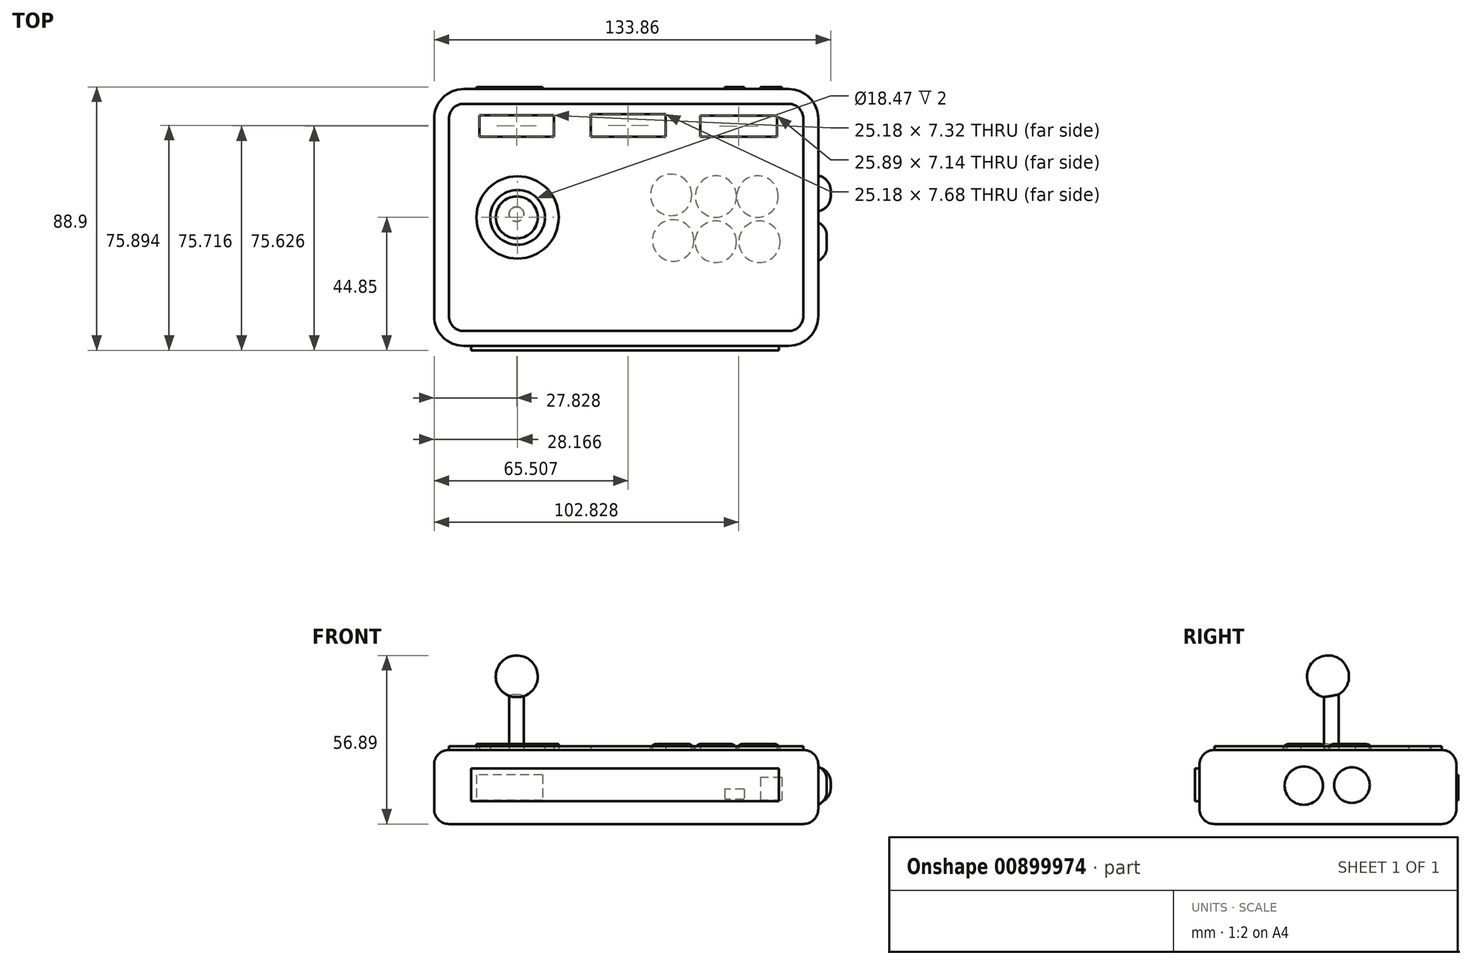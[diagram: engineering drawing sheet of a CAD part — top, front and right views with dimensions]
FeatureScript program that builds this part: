
annotation { "Feature Type Name" : "Feature", "Feature Type Description" : "" }
export const myFeature = defineFeature(function(context is Context, id is Id, definition is map)
    precondition{}
    {
        {
            var Q0;
            Q0=qCreatedBy(makeId("Top.planeOp"),FACE);
            var sketch = newSketch(context, id + "F0", { "sketchPlane" : qUnion([Q0])});
            skLineSegment(sketch, "E0.bottom", {"start": v(64.83, -43.35) * mm, "end": v(-64.83, -43.35) * mm});
            skLineSegment(sketch, "E0.top", {"start": v(64.83, 43.35) * mm, "end": v(-64.83, 43.35) * mm});
            skLineSegment(sketch, "E0.left", {"start": v(64.83, -43.35) * mm, "end": v(64.83, 43.35) * mm});
            skLineSegment(sketch, "E0.right", {"start": v(-64.83, -43.35) * mm, "end": v(-64.83, 43.35) * mm});
            skPoint(sketch, "E0.middle", {"position": v(0, 0) * mm});
            skSolve(sketch);
        }
        {
            var Q0;
            Q0 = qSketchRegion(id + "F0", true);
            extrude(context, id + "F1", {"entities" : qUnion([Q0]), "depth" : 25 * mm, "offsetDistance" : 25 * mm});
        }
        {
            var Q0;
            Q0=makeQuery(id+"F1.opExtrude","SWEPT_EDGE",EDGE,{"disambiguationData":[OSD([sQuery(id+"F0.wireOp",EDGE,"E0.bottom"),sQuery(id+"F0.wireOp",EDGE,"E0.right")])]});
            var Q1;
            Q1=makeQuery(id+"F1.opExtrude","SWEPT_EDGE",EDGE,{"disambiguationData":[OSD([sQuery(id+"F0.wireOp",EDGE,"E0.top"),sQuery(id+"F0.wireOp",EDGE,"E0.right")])]});
            var Q2;
            Q2=makeQuery(id+"F1.opExtrude","SWEPT_EDGE",EDGE,{"disambiguationData":[OSD([sQuery(id+"F0.wireOp",EDGE,"E0.bottom"),sQuery(id+"F0.wireOp",EDGE,"E0.left")])]});
            var Q3;
            Q3=makeQuery(id+"F1.opExtrude","SWEPT_EDGE",EDGE,{"disambiguationData":[OSD([sQuery(id+"F0.wireOp",EDGE,"E0.top"),sQuery(id+"F0.wireOp",EDGE,"E0.left")])]});
            fillet(context, id + "F2", {"entities" : qUnion([Q0, Q1, Q2, Q3]), "radius" : 10 * mm, "tangentPropagation" : true, "allowEdgeOverflow" : false});
        }
        {
            var Q0;
            Q0=makeQuery(id+"F1.opExtrude","CAP_FACE",FACE,{"disambiguationData":[OSD([sQuery(id+"F0.wireOp",EDGE,"E0.bottom"),sQuery(id+"F0.wireOp",EDGE,"E0.top"),sQuery(id+"F0.wireOp",EDGE,"E0.left"),sQuery(id+"F0.wireOp",EDGE,"E0.right")])],"isStart":false});
            var Q1;
            Q1=makeQuery(id+"F1.opExtrude","CAP_FACE",FACE,{"disambiguationData":[OSD([sQuery(id+"F0.wireOp",EDGE,"E0.bottom"),sQuery(id+"F0.wireOp",EDGE,"E0.top"),sQuery(id+"F0.wireOp",EDGE,"E0.left"),sQuery(id+"F0.wireOp",EDGE,"E0.right")])],"isStart":true});
            fillet(context, id + "F3", {"entities" : qUnion([Q0, Q1]), "radius" : 5 * mm, "tangentPropagation" : true, "allowEdgeOverflow" : false});
        }
        {
            var Q0;
            Q0=makeQuery(id+"F1.opExtrude","CAP_FACE",FACE,{"disambiguationData":[OSD([sQuery(id+"F0.wireOp",EDGE,"E0.bottom"),sQuery(id+"F0.wireOp",EDGE,"E0.top"),sQuery(id+"F0.wireOp",EDGE,"E0.left"),sQuery(id+"F0.wireOp",EDGE,"E0.right")])],"isStart":false});
            var sketch = newSketch(context, id + "F4", { "sketchPlane" : qUnion([Q0])});
            skCircle(sketch, "E1", {"center": v(-36.66, 0) * mm, "radius": 9.23 * mm});
            skCircle(sketch, "E2", {"center": v(-36.66, 0) * mm, "radius": 13.9 * mm});
            skCircle(sketch, "E3", {"center": v(15.89, -7.78) * mm, "radius": 7 * mm});
            skCircle(sketch, "E4", {"center": v(30.25, -8.22) * mm, "radius": 7 * mm});
            skCircle(sketch, "E5", {"center": v(45, -8.22) * mm, "radius": 7 * mm});
            skCircle(sketch, "E6", {"center": v(15.18, 7.6) * mm, "radius": 7 * mm});
            skCircle(sketch, "E7", {"center": v(30.29, 7.07) * mm, "radius": 7 * mm});
            skCircle(sketch, "E8", {"center": v(44.34, 7.07) * mm, "radius": 7 * mm});
            skPoint(sketch, "E9.middle", {"position": v(-54.83, 33.35) * mm});
            skSolve(sketch);
        }
        {
            var Q0;
            Q0=makeQuery(id+"F4.imprint","IMPRINT",FACE,{"disambiguationData":[TD([[makeQuery(id+"F4.imprint","IMPRINT",EDGE,{"derivedFrom":sQuery(id+"F4.wireOp",EDGE,"E6")}),1.0]])]});
            var Q1;
            Q1=makeQuery(id+"F4.imprint","IMPRINT",FACE,{"disambiguationData":[TD([[makeQuery(id+"F4.imprint","IMPRINT",EDGE,{"derivedFrom":sQuery(id+"F4.wireOp",EDGE,"E7")}),1.0]])]});
            var Q2;
            Q2=makeQuery(id+"F4.imprint","IMPRINT",FACE,{"disambiguationData":[TD([[makeQuery(id+"F4.imprint","IMPRINT",EDGE,{"derivedFrom":sQuery(id+"F4.wireOp",EDGE,"E8")}),1.0]])]});
            var Q3;
            Q3=makeQuery(id+"F4.imprint","IMPRINT",FACE,{"disambiguationData":[TD([[makeQuery(id+"F4.imprint","IMPRINT",EDGE,{"derivedFrom":sQuery(id+"F4.wireOp",EDGE,"E3")}),1.0]])]});
            var Q4;
            Q4=makeQuery(id+"F4.imprint","IMPRINT",FACE,{"disambiguationData":[TD([[makeQuery(id+"F4.imprint","IMPRINT",EDGE,{"derivedFrom":sQuery(id+"F4.wireOp",EDGE,"E4")}),1.0]])]});
            var Q5;
            Q5=makeQuery(id+"F4.imprint","IMPRINT",FACE,{"disambiguationData":[TD([[makeQuery(id+"F4.imprint","IMPRINT",EDGE,{"derivedFrom":sQuery(id+"F4.wireOp",EDGE,"E5")}),1.0]])]});
            var Q6;
            Q6=makeQuery(id+"F4.imprint","IMPRINT",FACE,{"disambiguationData":[TD([[makeQuery(id+"F4.imprint","IMPRINT",EDGE,{"derivedFrom":sQuery(id+"F4.wireOp",EDGE,"E1")}),-1.0]])]});
            extrude(context, id + "F5", {"entities" : qUnion([Q0, Q1, Q2, Q3, Q4, Q5, Q6]), "depth" : 2 * mm, "offsetDistance" : 25 * mm});
        }
        {
            var Q0;
            Q0=makeQuery(id+"F5.opExtrude","CAP_EDGE",EDGE,{"disambiguationData":[OSD([sQuery(id+"F4.wireOp",EDGE,"E3")])],"isStart":false});
            var Q1;
            Q1=makeQuery(id+"F5.opExtrude","CAP_FACE",FACE,{"disambiguationData":[OSD([sQuery(id+"F4.wireOp",EDGE,"E4")])],"isStart":false});
            var Q2;
            Q2=makeQuery(id+"F5.opExtrude","CAP_EDGE",EDGE,{"disambiguationData":[OSD([sQuery(id+"F4.wireOp",EDGE,"E5")])],"isStart":false});
            var Q3;
            Q3=makeQuery(id+"F5.opExtrude","CAP_EDGE",EDGE,{"disambiguationData":[OSD([sQuery(id+"F4.wireOp",EDGE,"E8")])],"isStart":false});
            var Q4;
            Q4=makeQuery(id+"F5.opExtrude","CAP_EDGE",EDGE,{"disambiguationData":[OSD([sQuery(id+"F4.wireOp",EDGE,"E7")])],"isStart":false});
            var Q5;
            Q5=makeQuery(id+"F5.opExtrude","CAP_EDGE",EDGE,{"disambiguationData":[OSD([sQuery(id+"F4.wireOp",EDGE,"E6")])],"isStart":false});
            fillet(context, id + "F6", {"entities" : qUnion([Q0, Q1, Q2, Q3, Q4, Q5]), "radius" : 2 * mm, "tangentPropagation" : true, "allowEdgeOverflow" : false});
        }
        {
            var Q0;
            Q0=makeQuery(id+"F4.imprint","IMPRINT",FACE,{"disambiguationData":[TD([[makeQuery(id+"F4.imprint","IMPRINT",EDGE,{"derivedFrom":sQuery(id+"F4.wireOp",EDGE,"E1")}),1.0]])]});
            var sketch = newSketch(context, id + "F7", { "sketchPlane" : qUnion([Q0])});
            skCircle(sketch, "E10", {"center": v(-37.03, 1.1) * mm, "radius": 2.5 * mm});
            skSolve(sketch);
        }
        {
            var Q0;
            Q0=makeQuery(id+"F7.imprint","IMPRINT",FACE,{"disambiguationData":[TD([[makeQuery(id+"F7.imprint","IMPRINT",EDGE,{"derivedFrom":sQuery(id+"F7.wireOp",EDGE,"E10")}),1.0]])]});
            extrude(context, id + "F8", {"entities" : qUnion([Q0]), "operationType" : NewBodyOperationType.ADD, "depth" : 18.6 * mm, "offsetDistance" : 25 * mm});
        }
        {
            var Q0;
            Q0=qCreatedBy(makeId("Front.planeOp"),FACE);
            var sketch = newSketch(context, id + "F9", { "sketchPlane" : qUnion([Q0])});
            skArc(sketch, "E11", {"start": v(-36.94, 42.72) * mm, "mid": v(-29.86, 49.8) * mm, "end": v(-36.94, 56.89) * mm});
            skLineSegment(sketch, "E12", {"start": v(-36.94, 49.8) * mm, "end": v(-36.94, 56.89) * mm});
            skLineSegment(sketch, "E13", {"start": v(-36.94, 49.8) * mm, "end": v(-36.94, 42.72) * mm});
            skSolve(sketch);
        }
        {
            var Q0;
            Q0=makeQuery(id+"F9.imprint","IMPRINT",FACE,{"disambiguationData":[TD([[makeQuery(id+"F9.imprint","IMPRINT",EDGE,{"derivedFrom":sQuery(id+"F9.wireOp",EDGE,"E11")}),1.0]])]});
            var Q1;
            Q1=sQuery(id+"F9.wireOp",EDGE,"E12");
            revolve(context, id + "F10", {"operationType" : NewBodyOperationType.ADD, "surfaceOperationType" : NewSurfaceOperationType.NEW, "entities" : qUnion([Q0]), "axis" : qUnion([Q1]), "revolveType" : RevolveType.FULL});
        }
        {
            var Q0;
            Q0=makeQuery(id+"F1.opExtrude","SWEPT_FACE",FACE,{"disambiguationData":[OSD([sQuery(id+"F0.wireOp",EDGE,"E0.left")])]});
            var sketch = newSketch(context, id + "F11", { "sketchPlane" : qUnion([Q0])});
            skCircle(sketch, "E14", {"center": v(-8.16, 12.94) * mm, "radius": 6.46 * mm});
            skSolve(sketch);
        }
        {
            var Q0;
            Q0 = qSketchRegion(id + "F11", true);
            extrude(context, id + "F12", {"entities" : qUnion([Q0]), "operationType" : NewBodyOperationType.ADD, "depth" : 2.9 * mm, "offsetDistance" : 25 * mm});
        }
        {
            var Q0;
            Q0=makeQuery(id+"F12.opExtrude","CAP_EDGE",EDGE,{"disambiguationData":[OSD([sQuery(id+"F11.wireOp",EDGE,"E14")])],"isStart":false});
            fillet(context, id + "F13", {"entities" : qUnion([Q0]), "radius" : 5 * mm, "tangentPropagation" : true, "allowEdgeOverflow" : false});
        }
        {
            var Q0;
            Q0=makeQuery(id+"F11.imprint","IMPRINT",FACE,{"disambiguationData":[TD([[makeQuery(id+"F11.imprint","IMPRINT",EDGE,{"derivedFrom":sQuery(id+"F11.wireOp",EDGE,"E14")}),-1.0]])]});
            var sketch = newSketch(context, id + "F14", { "sketchPlane" : qUnion([Q0])});
            skCircle(sketch, "E15", {"center": v(8.1, 13.11) * mm, "radius": 6 * mm});
            skSolve(sketch);
        }
        {
            var Q0;
            Q0=makeQuery(id+"F14.imprint","IMPRINT",FACE,{"disambiguationData":[TD([[makeQuery(id+"F14.imprint","IMPRINT",EDGE,{"derivedFrom":sQuery(id+"F14.wireOp",EDGE,"E15")}),1.0]])]});
            extrude(context, id + "F15", {"entities" : qUnion([Q0]), "operationType" : NewBodyOperationType.ADD, "depth" : 4.2 * mm, "offsetDistance" : 25 * mm});
        }
        {
            var Q0;
            Q0=makeQuery(id+"F15.opExtrude","CAP_EDGE",EDGE,{"disambiguationData":[OSD([sQuery(id+"F14.wireOp",EDGE,"E15")])],"isStart":false});
            fillet(context, id + "F16", {"entities" : qUnion([Q0]), "radius" : 5 * mm, "tangentPropagation" : true, "allowEdgeOverflow" : false});
        }
        {
            var Q0;
            Q0=makeQuery(id+"F4.imprint","IMPRINT",FACE,{"disambiguationData":[TD([[makeQuery(id+"F4.imprint","IMPRINT",EDGE,{"derivedFrom":sQuery(id+"F4.wireOp",EDGE,"E2")}),-1.0]])]});
            var sketch = newSketch(context, id + "F17", { "sketchPlane" : qUnion([Q0])});
            skLineSegment(sketch, "E16.bottom", {"start": v(-49.6, 34.53) * mm, "end": v(-24.41, 34.53) * mm});
            skLineSegment(sketch, "E16.top", {"start": v(-49.6, 27.2) * mm, "end": v(-24.41, 27.2) * mm});
            skLineSegment(sketch, "E16.left", {"start": v(-49.6, 34.53) * mm, "end": v(-49.6, 27.2) * mm});
            skLineSegment(sketch, "E16.right", {"start": v(-24.41, 34.53) * mm, "end": v(-24.41, 27.2) * mm});
            skLineSegment(sketch, "E17.bottom", {"start": v(25.05, 34.35) * mm, "end": v(50.94, 34.35) * mm});
            skLineSegment(sketch, "E17.top", {"start": v(25.05, 27.2) * mm, "end": v(50.94, 27.2) * mm});
            skLineSegment(sketch, "E17.left", {"start": v(25.05, 34.35) * mm, "end": v(25.05, 27.2) * mm});
            skLineSegment(sketch, "E17.right", {"start": v(50.94, 34.35) * mm, "end": v(50.94, 27.2) * mm});
            skLineSegment(sketch, "E18.bottom", {"start": v(-11.91, 34.88) * mm, "end": v(13.27, 34.88) * mm});
            skLineSegment(sketch, "E18.top", {"start": v(-11.91, 27.2) * mm, "end": v(13.27, 27.2) * mm});
            skLineSegment(sketch, "E18.left", {"start": v(-11.91, 34.88) * mm, "end": v(-11.91, 27.2) * mm});
            skLineSegment(sketch, "E18.right", {"start": v(13.27, 34.88) * mm, "end": v(13.27, 27.2) * mm});
            skLineSegment(sketch, "E19.0.0", {"start": v(-59.83, 33.35) * mm, "end": v(-59.83, -33.35) * mm});
            skArc(sketch, "E19.0.1", {"start": v(-59.83, -33.35) * mm, "mid": v(-58.37, -36.89) * mm, "end": v(-54.83, -38.35) * mm});
            skLineSegment(sketch, "E19.0.2", {"start": v(-54.83, -38.35) * mm, "end": v(54.83, -38.35) * mm});
            skArc(sketch, "E19.0.3", {"start": v(54.83, -38.35) * mm, "mid": v(58.37, -36.89) * mm, "end": v(59.83, -33.35) * mm});
            skLineSegment(sketch, "E19.0.4", {"start": v(59.83, -33.35) * mm, "end": v(59.83, 33.35) * mm});
            skArc(sketch, "E19.0.5", {"start": v(59.83, 33.35) * mm, "mid": v(58.37, 36.89) * mm, "end": v(54.83, 38.35) * mm});
            skLineSegment(sketch, "E19.0.6", {"start": v(54.83, 38.35) * mm, "end": v(-54.83, 38.35) * mm});
            skArc(sketch, "E19.0.7", {"start": v(-54.83, 38.35) * mm, "mid": v(-58.37, 36.89) * mm, "end": v(-59.83, 33.35) * mm});
            skSolve(sketch);
        }
        {
            var Q0;
            Q0 = qSketchRegion(id + "F17", true);
            extrude(context, id + "F18", {"entities" : qUnion([Q0]), "depth" : 1.3 * mm, "offsetDistance" : 25 * mm});
        }
        {
            var Q0;
            Q0=makeQuery(id+"F1.opExtrude","SWEPT_FACE",FACE,{"disambiguationData":[OSD([sQuery(id+"F0.wireOp",EDGE,"E0.top")])]});
            var sketch = newSketch(context, id + "F19", { "sketchPlane" : qUnion([Q0])});
            skLineSegment(sketch, "E20.bottom", {"start": v(28.2, 16.58) * mm, "end": v(50.6, 16.58) * mm});
            skLineSegment(sketch, "E20.top", {"start": v(28.2, 7.94) * mm, "end": v(50.6, 7.94) * mm});
            skLineSegment(sketch, "E20.left", {"start": v(28.2, 16.58) * mm, "end": v(28.2, 7.94) * mm});
            skLineSegment(sketch, "E20.right", {"start": v(50.6, 16.58) * mm, "end": v(50.6, 7.94) * mm});
            skPoint(sketch, "E21.oppositeSnap0", {"position": v(39.4, 7.94) * mm});
            skLineSegment(sketch, "E21.bottom", {"start": v(-52.63, 15.65) * mm, "end": v(-45.32, 15.65) * mm});
            skLineSegment(sketch, "E21.top", {"start": v(-52.63, 7.94) * mm, "end": v(-45.32, 7.94) * mm});
            skLineSegment(sketch, "E21.left", {"start": v(-52.63, 15.65) * mm, "end": v(-52.63, 7.94) * mm});
            skLineSegment(sketch, "E21.right", {"start": v(-45.32, 15.65) * mm, "end": v(-45.32, 7.94) * mm});
            skLineSegment(sketch, "E22.bottom", {"start": v(-39.89, 11.75) * mm, "end": v(-33.33, 11.75) * mm});
            skLineSegment(sketch, "E22.top", {"start": v(-39.89, 8.28) * mm, "end": v(-33.33, 8.28) * mm});
            skLineSegment(sketch, "E22.left", {"start": v(-39.89, 11.75) * mm, "end": v(-39.89, 8.28) * mm});
            skLineSegment(sketch, "E22.right", {"start": v(-33.33, 11.75) * mm, "end": v(-33.33, 8.28) * mm});
            skSolve(sketch);
        }
        {
            var Q0;
            Q0 = qSketchRegion(id + "F19", true);
            extrude(context, id + "F20", {"entities" : qUnion([Q0]), "operationType" : NewBodyOperationType.ADD, "depth" : 0.7 * mm, "offsetDistance" : 25 * mm});
        }
        {
            var Q0;
            Q0=makeQuery(id+"F1.opExtrude","SWEPT_FACE",FACE,{"disambiguationData":[OSD([sQuery(id+"F0.wireOp",EDGE,"E0.bottom")])]});
            var sketch = newSketch(context, id + "F21", { "sketchPlane" : qUnion([Q0])});
            skLineSegment(sketch, "E23.bottom", {"start": v(-52.36, 18.74) * mm, "end": v(51.57, 18.74) * mm});
            skLineSegment(sketch, "E23.top", {"start": v(-52.36, 7.7) * mm, "end": v(51.57, 7.7) * mm});
            skLineSegment(sketch, "E23.left", {"start": v(-52.36, 18.74) * mm, "end": v(-52.36, 7.7) * mm});
            skLineSegment(sketch, "E23.right", {"start": v(51.57, 18.74) * mm, "end": v(51.57, 7.7) * mm});
            skSolve(sketch);
        }
        {
            var Q0;
            Q0 = qSketchRegion(id + "F21", true);
            extrude(context, id + "F22", {"entities" : qUnion([Q0]), "operationType" : NewBodyOperationType.ADD, "depth" : 1.5 * mm, "offsetDistance" : 25 * mm});
        }
    });
